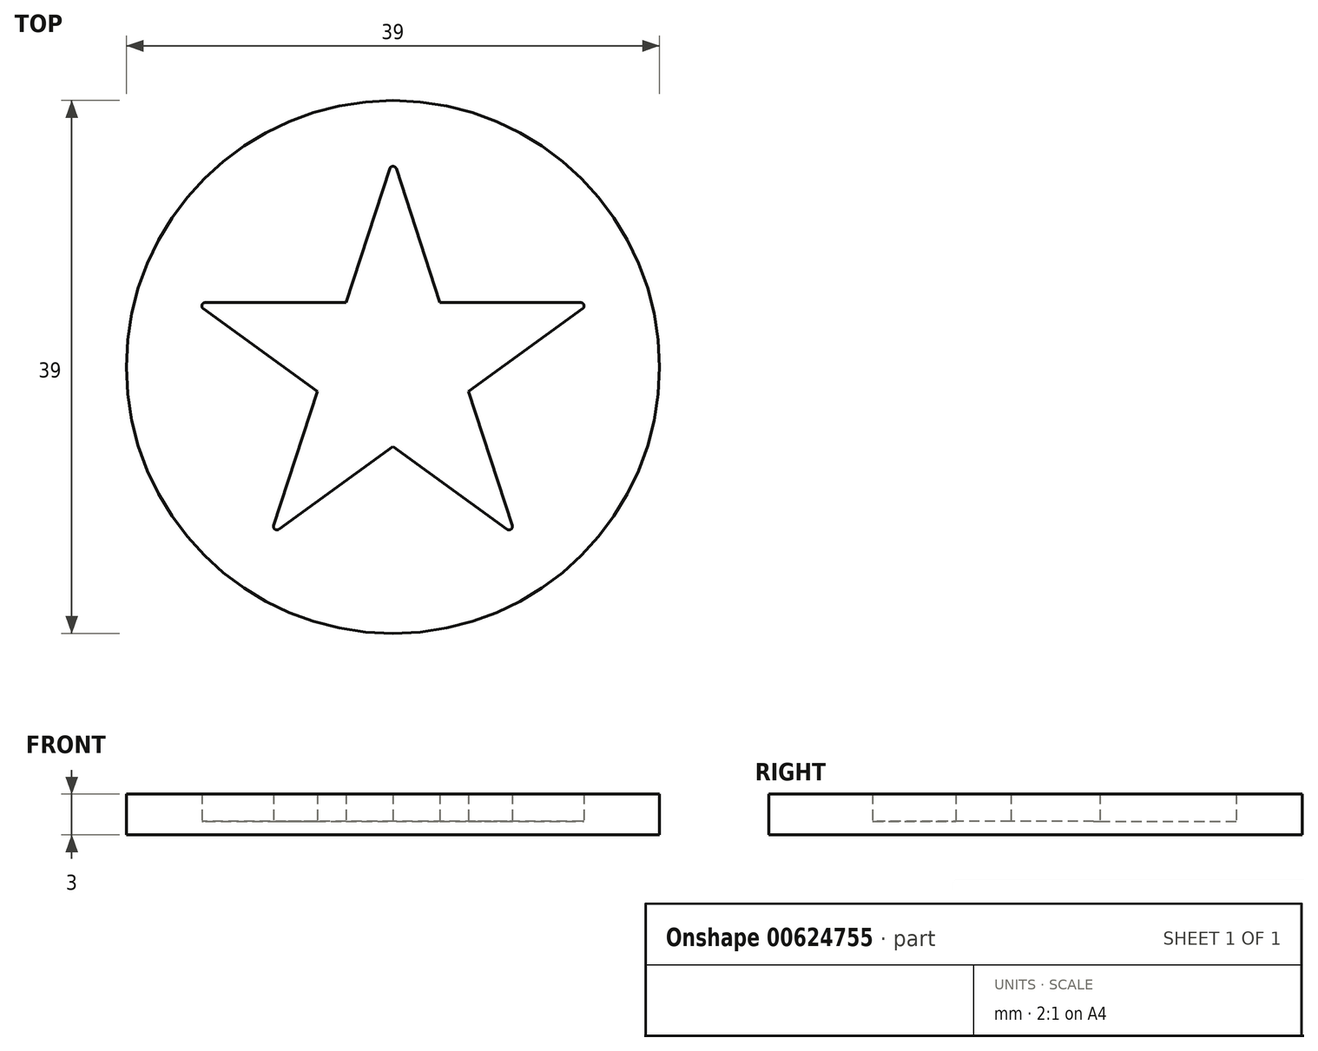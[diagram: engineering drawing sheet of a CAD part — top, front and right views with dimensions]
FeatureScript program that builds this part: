
annotation { "Feature Type Name" : "Feature", "Feature Type Description" : "" }
export const myFeature = defineFeature(function(context is Context, id is Id, definition is map)
    precondition{}
    {
        {
            var Q0;
            Q0=qCreatedBy(makeId("Top.planeOp"),FACE);
            var sketch = newSketch(context, id + "F0", { "sketchPlane" : qUnion([Q0])});
            skLineSegment(sketch, "E0", {"start": v(-8.72, -11.6) * mm, "end": v(-0.24, 14.51) * mm});
            skLineSegment(sketch, "E1", {"start": v(0.24, 14.51) * mm, "end": v(8.72, -11.6) * mm});
            skLineSegment(sketch, "E2", {"start": v(8.34, -11.88) * mm, "end": v(-13.88, 4.26) * mm});
            skLineSegment(sketch, "E3", {"start": v(-13.73, 4.71) * mm, "end": v(13.73, 4.71) * mm});
            skLineSegment(sketch, "E4", {"start": v(13.88, 4.26) * mm, "end": v(-8.34, -11.88) * mm});
            skLineSegment(sketch, "E5", {"start": v(0, -5.82) * mm, "end": v(0, 4.71) * mm, "construction": true});
            skCircle(sketch, "E6", {"center": v(0, 0) * mm, "radius": 19.5 * mm});
            skLineSegment(sketch, "E7", {"start": v(5.54, -1.8) * mm, "end": v(-4.48, 1.46) * mm, "construction": true});
            skLineSegment(sketch, "E8", {"start": v(3.42, 4.71) * mm, "end": v(-2.77, -3.81) * mm, "construction": true});
            skLineSegment(sketch, "E9", {"start": v(-3.42, 4.71) * mm, "end": v(2.77, -3.81) * mm, "construction": true});
            skLineSegment(sketch, "E10", {"start": v(-5.54, -1.8) * mm, "end": v(4.48, 1.46) * mm, "construction": true});
            skPoint(sketch, "E11.visualSharp", {"position": v(0, 15.25) * mm});
            skArc(sketch, "E11.filletArc", {"start": v(0.24, 14.51) * mm, "mid": v(0, 14.69) * mm, "end": v(-0.24, 14.51) * mm});
            skPoint(sketch, "E12.visualSharp", {"position": v(14.5, 4.71) * mm});
            skArc(sketch, "E12.filletArc", {"start": v(13.88, 4.26) * mm, "mid": v(13.97, 4.54) * mm, "end": v(13.73, 4.71) * mm});
            skPoint(sketch, "E13.visualSharp", {"position": v(8.96, -12.33) * mm});
            skArc(sketch, "E13.filletArc", {"start": v(8.34, -11.88) * mm, "mid": v(8.63, -11.88) * mm, "end": v(8.72, -11.6) * mm});
            skPoint(sketch, "E14.visualSharp", {"position": v(-8.96, -12.33) * mm});
            skArc(sketch, "E14.filletArc", {"start": v(-8.72, -11.6) * mm, "mid": v(-8.63, -11.88) * mm, "end": v(-8.34, -11.88) * mm});
            skPoint(sketch, "E15.visualSharp", {"position": v(-14.5, 4.71) * mm});
            skArc(sketch, "E15.filletArc", {"start": v(-13.73, 4.71) * mm, "mid": v(-13.97, 4.54) * mm, "end": v(-13.88, 4.26) * mm});
            skSolve(sketch);
        }
        {
            var Q0;
            Q0=makeQuery(id+"F0.imprint","IMPRINT",FACE,{"disambiguationData":[TD([[makeQuery(id+"F0.imprint","IMPRINT",EDGE,{"derivedFrom":sQuery(id+"F0.wireOp",EDGE,"E6")}),1.0]])]});
            extrude(context, id + "F1", {"entities" : qUnion([Q0]), "depth" : 3 * mm});
        }
        {
            var Q0;
            {var subQ0=sQuery(id+"F0.wireOp",EDGE,"E2");var subQ1=sQuery(id+"F0.wireOp",EDGE,"E0");var subQ2=makeQuery(id+"F0.imprint","INTERSECT",VERTEX,{"derivedFrom":[subQ1,subQ0]});Q0=makeQuery(id+"F0.imprint","IMPRINT",FACE,{"disambiguationData":[TD([[makeQuery(id+"F0.imprint","IMPRINT",EDGE,{"disambiguationData":[TD([[subQ2,-1.0]])],"derivedFrom":subQ1}),1.0]])]});}
            var Q1;
            {var subQ0=sQuery(id+"F0.wireOp",EDGE,"E1");var subQ1=sQuery(id+"F0.wireOp",EDGE,"E0");var subQ2=makeQuery(id+"F0.imprint","INTERSECT",VERTEX,{"derivedFrom":[subQ1,subQ0]});Q1=makeQuery(id+"F0.imprint","IMPRINT",FACE,{"disambiguationData":[TD([[makeQuery(id+"F0.imprint","IMPRINT",EDGE,{"disambiguationData":[TD([[subQ2,1.0]])],"derivedFrom":subQ1}),-1.0]])]});}
            var Q2;
            {var subQ0=sQuery(id+"F0.wireOp",EDGE,"E3");var subQ1=sQuery(id+"F0.wireOp",EDGE,"E1");var subQ2=makeQuery(id+"F0.imprint","INTERSECT",VERTEX,{"derivedFrom":[subQ1,subQ0]});Q2=makeQuery(id+"F0.imprint","IMPRINT",FACE,{"disambiguationData":[TD([[makeQuery(id+"F0.imprint","IMPRINT",EDGE,{"disambiguationData":[TD([[subQ2,-1.0]])],"derivedFrom":subQ1}),1.0]])]});}
            var Q3;
            {var subQ1=sQuery(id+"F0.wireOp",EDGE,"E0");var subQ5=sQuery(id+"F0.wireOp",EDGE,"E2");var subQ6=makeQuery(id+"F0.imprint","INTERSECT",VERTEX,{"derivedFrom":[subQ1,subQ5]});Q3=makeQuery(id+"F0.imprint","IMPRINT",FACE,{"disambiguationData":[TD([[makeQuery(id+"F0.imprint","IMPRINT",EDGE,{"disambiguationData":[TD([[subQ6,-1.0]])],"derivedFrom":subQ1}),-1.0]])]});}
            var Q4;
            {var subQ0=sQuery(id+"F0.wireOp",EDGE,"E2");var subQ1=sQuery(id+"F0.wireOp",EDGE,"E1");var subQ2=makeQuery(id+"F0.imprint","INTERSECT",VERTEX,{"derivedFrom":[subQ1,subQ0]});Q4=makeQuery(id+"F0.imprint","IMPRINT",FACE,{"disambiguationData":[TD([[makeQuery(id+"F0.imprint","IMPRINT",EDGE,{"disambiguationData":[TD([[subQ2,1.0]])],"derivedFrom":subQ1}),-1.0]])]});}
            var Q5;
            {var subQ0=sQuery(id+"F0.wireOp",EDGE,"E4");var subQ1=sQuery(id+"F0.wireOp",EDGE,"E0");var subQ2=makeQuery(id+"F0.imprint","INTERSECT",VERTEX,{"derivedFrom":[subQ1,subQ0]});Q5=makeQuery(id+"F0.imprint","IMPRINT",FACE,{"disambiguationData":[TD([[makeQuery(id+"F0.imprint","IMPRINT",EDGE,{"disambiguationData":[TD([[subQ2,-1.0]])],"derivedFrom":subQ1}),-1.0]])]});}
            extrude(context, id + "F2", {"entities" : qUnion([Q0, Q1, Q2, Q3, Q4, Q5]), "operationType" : NewBodyOperationType.ADD, "depth" : 1 * mm});
        }
    });
